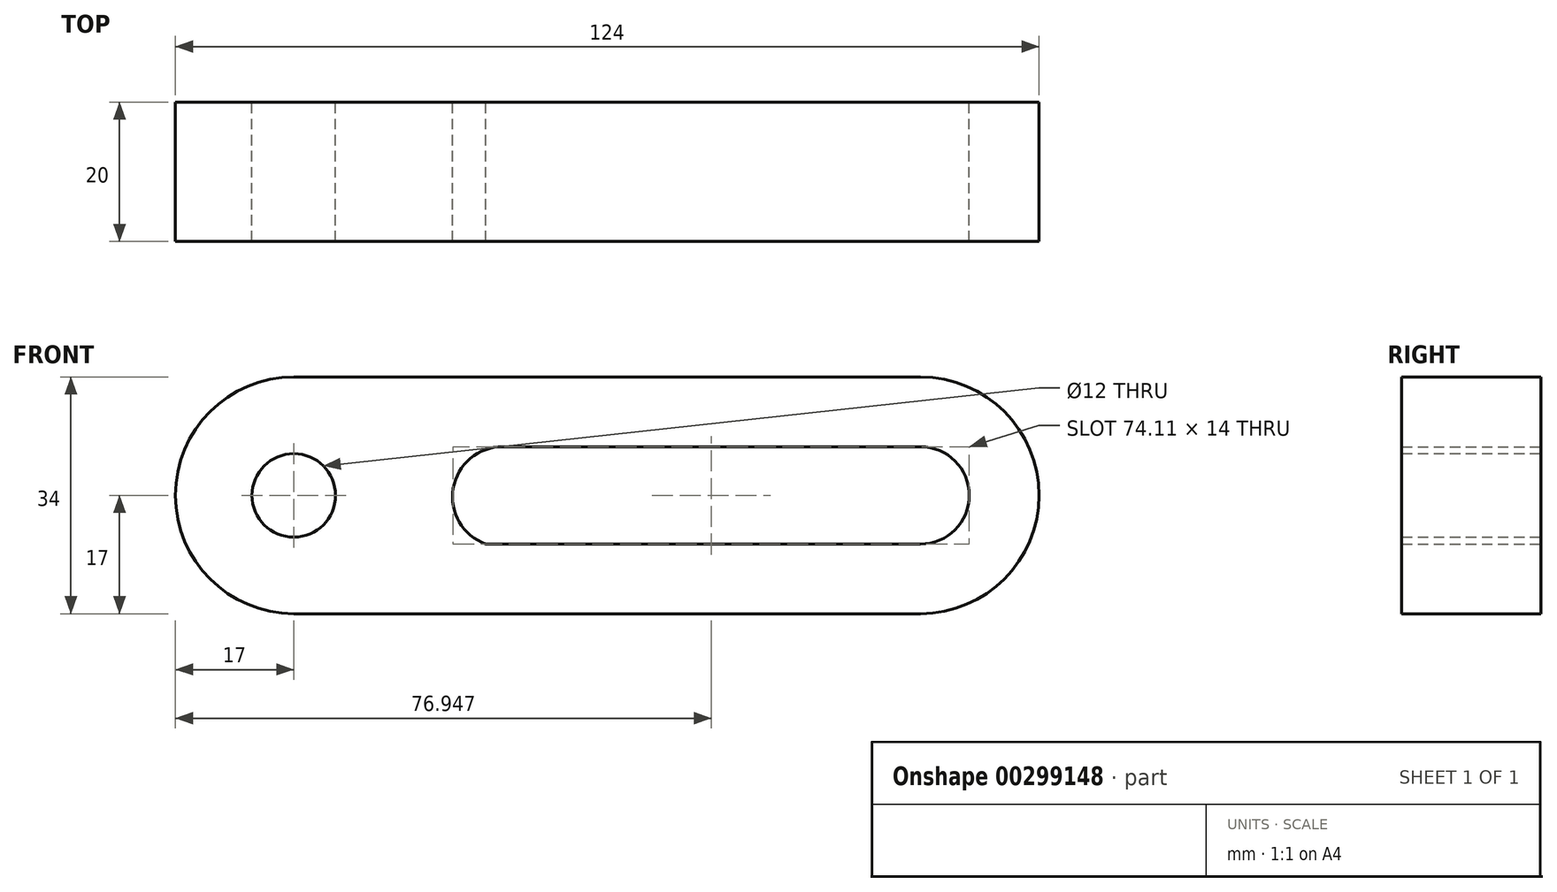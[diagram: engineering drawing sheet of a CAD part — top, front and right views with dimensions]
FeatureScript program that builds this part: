
annotation { "Feature Type Name" : "Feature", "Feature Type Description" : "" }
export const myFeature = defineFeature(function(context is Context, id is Id, definition is map)
    precondition{}
    {
        {
            var Q0;
            Q0=qCreatedBy(makeId("Front.planeOp"),FACE);
            var sketch = newSketch(context, id + "F0", { "sketchPlane" : qUnion([Q0])});
            skLineSegment(sketch, "E0", {"start": v(0, 34) * mm, "end": v(90, 34) * mm});
            skLineSegment(sketch, "E1", {"start": v(0, 0) * mm, "end": v(90, 0) * mm});
            skArc(sketch, "E2", {"start": v(0, 34) * mm, "mid": v(-17, 17) * mm, "end": v(0, 0) * mm});
            skArc(sketch, "E3", {"start": v(90, 34) * mm, "mid": v(107, 17) * mm, "end": v(90, 0) * mm});
            skCircle(sketch, "E4", {"center": v(0, 17) * mm, "radius": 6 * mm});
            skLineSegment(sketch, "E5", {"start": v(30, 24) * mm, "end": v(90, 24) * mm});
            skLineSegment(sketch, "E6", {"start": v(27.57, 10) * mm, "end": v(90, 10) * mm});
            skArc(sketch, "E7", {"start": v(90, 24) * mm, "mid": v(97, 17) * mm, "end": v(90, 10) * mm});
            skArc(sketch, "E8", {"start": v(30, 24) * mm, "mid": v(22.9, 18.02) * mm, "end": v(27.57, 10) * mm});
            skSolve(sketch);
        }
        {
            var Q0;
            Q0=qSketchRegion(id+"F0",true);
            extrude(context, id + "F1", {"entities" : qUnion([Q0]), "depth" : 20 * mm});
        }
    });
